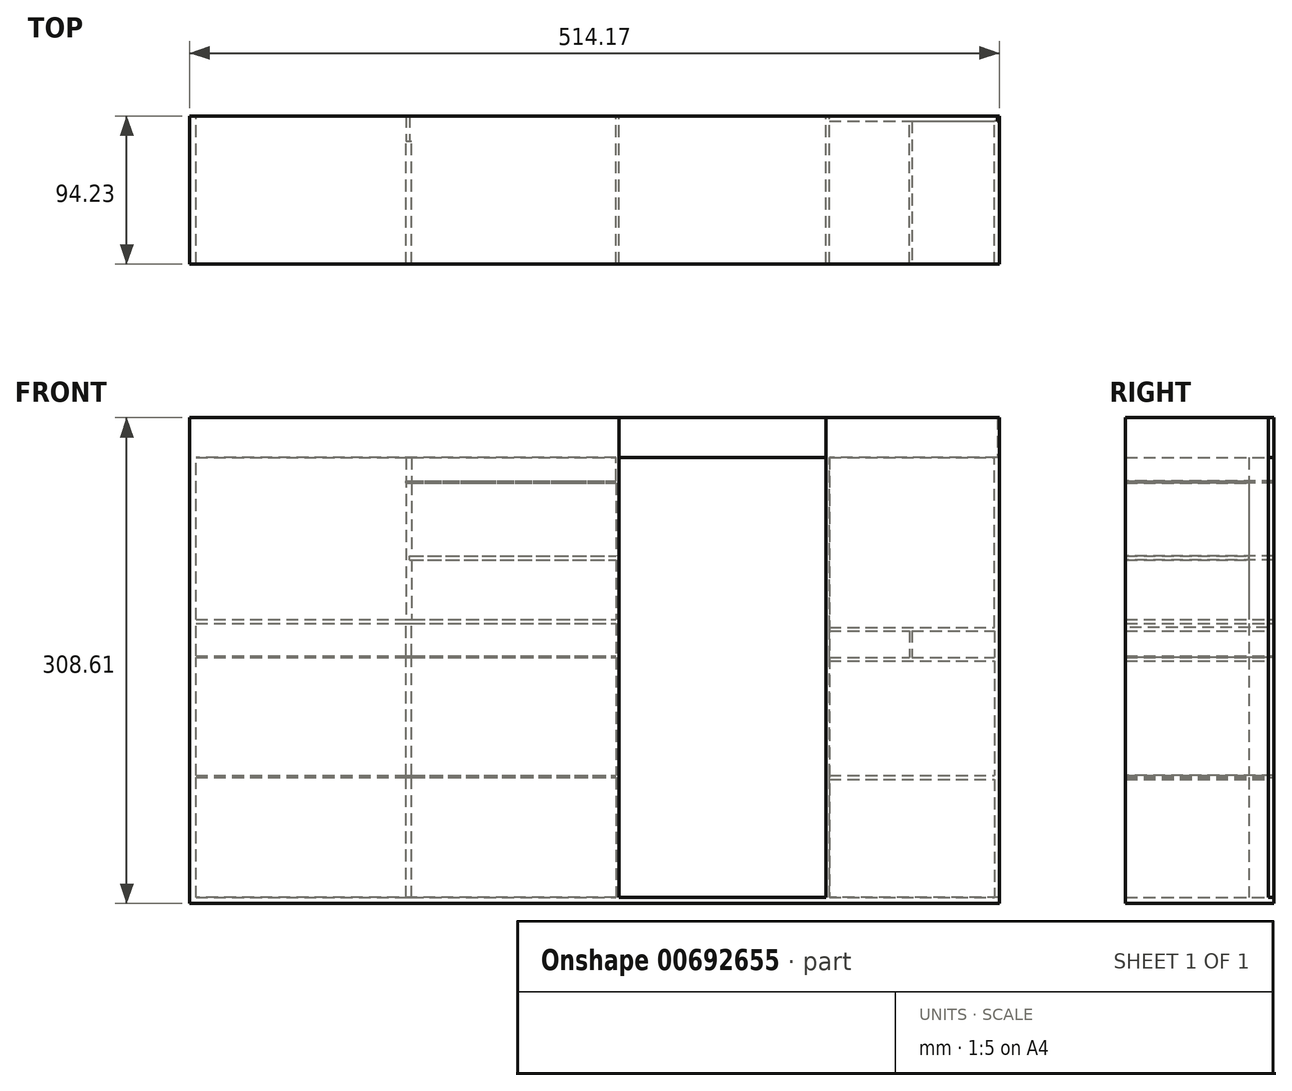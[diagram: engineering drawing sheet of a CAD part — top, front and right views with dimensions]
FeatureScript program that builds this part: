
annotation { "Feature Type Name" : "Feature", "Feature Type Description" : "" }
export const myFeature = defineFeature(function(context is Context, id is Id, definition is map)
    precondition{}
    {
        {
            var Q0;
            Q0=qCreatedBy(makeId("Top.planeOp"),FACE);
            var sketch = newSketch(context, id + "F0", { "sketchPlane" : qUnion([Q0])});
            skLineSegment(sketch, "E0.bottom", {"start": v(254.1, -132.08) * mm, "end": v(-260.07, -132.08) * mm});
            skLineSegment(sketch, "E0.top", {"start": v(254.1, -37.85) * mm, "end": v(-260.07, -37.85) * mm});
            skLineSegment(sketch, "E0.left", {"start": v(254.1, -132.08) * mm, "end": v(254.1, -37.85) * mm});
            skLineSegment(sketch, "E0.right", {"start": v(-260.07, -132.08) * mm, "end": v(-260.07, -37.85) * mm});
            skSolve(sketch);
        }
        {
            var Q0;
            Q0=makeQuery(id+"F0.imprint","IMPRINT",FACE,{"disambiguationData":[TD([[makeQuery(id+"F0.imprint","IMPRINT",EDGE,{"derivedFrom":sQuery(id+"F0.wireOp",EDGE,"E0.bottom")}),-1.0]])]});
            extrude(context, id + "F1", {"entities" : qUnion([Q0]), "depth" : 3.8 * mm, "offsetDistance" : 25.4 * mm});
        }
        {
            var Q0;
            Q0=makeQuery(id+"F1.opExtrude","CAP_FACE",FACE,{"disambiguationData":[OSD([sQuery(id+"F0.wireOp",EDGE,"E0.bottom"),sQuery(id+"F0.wireOp",EDGE,"E0.top"),sQuery(id+"F0.wireOp",EDGE,"E0.left"),sQuery(id+"F0.wireOp",EDGE,"E0.right")])],"isStart":false});
            var sketch = newSketch(context, id + "F2", { "sketchPlane" : qUnion([Q0])});
            skLineSegment(sketch, "E1.bottom", {"start": v(143.85, -132.08) * mm, "end": v(146.14, -132.08) * mm});
            skLineSegment(sketch, "E1.top", {"start": v(143.85, -37.85) * mm, "end": v(146.14, -37.85) * mm});
            skLineSegment(sketch, "E1.left", {"start": v(143.85, -132.08) * mm, "end": v(143.85, -37.85) * mm});
            skLineSegment(sketch, "E1.right", {"start": v(146.14, -132.08) * mm, "end": v(146.14, -37.85) * mm});
            skSolve(sketch);
        }
        {
            var Q0;
            Q0 = qSketchRegion(id + "F2", true);
            extrude(context, id + "F3", {"entities" : qUnion([Q0]), "operationType" : NewBodyOperationType.ADD, "depth" : 304.8 * mm, "offsetDistance" : 25.4 * mm});
        }
        {
            var Q0;
            {var subQ0=sQuery(id+"F0.wireOp",EDGE,"E0.left");var subQ1=sQuery(id+"F0.wireOp",EDGE,"E0.top");var subQ2=sQuery(id+"F0.wireOp",EDGE,"E0.bottom");Q0=makeQuery(id+"F3.boolean.opBoolean","SPLIT",FACE,{"disambiguationData":[TD([makeQuery(id+"F1.opExtrude","SWEPT_FACE",FACE,{"disambiguationData":[OSD([subQ0])]})])],"derivedFrom":makeQuery(id+"F1.opExtrude","CAP_FACE",FACE,{"disambiguationData":[OSD([subQ2,subQ1,subQ0,sQuery(id+"F0.wireOp",EDGE,"E0.right")])],"isStart":false})});}
            var sketch = newSketch(context, id + "F4", { "sketchPlane" : qUnion([Q0])});
            skLineSegment(sketch, "E2.bottom", {"start": v(254.1, -132.08) * mm, "end": v(250.9, -132.08) * mm});
            skLineSegment(sketch, "E2.top", {"start": v(254.1, -41.27) * mm, "end": v(250.9, -41.27) * mm});
            skLineSegment(sketch, "E2.left", {"start": v(254.1, -132.08) * mm, "end": v(254.1, -41.27) * mm});
            skLineSegment(sketch, "E2.right", {"start": v(250.9, -132.08) * mm, "end": v(250.9, -41.27) * mm});
            skSolve(sketch);
        }
        {
            var Q0;
            Q0 = qSketchRegion(id + "F4", true);
            extrude(context, id + "F5", {"entities" : qUnion([Q0]), "operationType" : NewBodyOperationType.ADD, "depth" : 304.8 * mm, "offsetDistance" : 25.4 * mm});
        }
        {
            var Q0;
            {var subQ0=sQuery(id+"F0.wireOp",EDGE,"E0.top");var subQ1=sQuery(id+"F0.wireOp",EDGE,"E0.right");var subQ2=sQuery(id+"F0.wireOp",EDGE,"E0.bottom");Q0=makeQuery(id+"F3.boolean.opBoolean","SPLIT",FACE,{"disambiguationData":[TD([makeQuery(id+"F1.opExtrude","SWEPT_FACE",FACE,{"disambiguationData":[OSD([subQ1])]})])],"derivedFrom":makeQuery(id+"F1.opExtrude","CAP_FACE",FACE,{"disambiguationData":[OSD([subQ2,subQ0,sQuery(id+"F0.wireOp",EDGE,"E0.left"),subQ1])],"isStart":false})});}
            var sketch = newSketch(context, id + "F6", { "sketchPlane" : qUnion([Q0])});
            skLineSegment(sketch, "E3.bottom", {"start": v(10.8, -132.08) * mm, "end": v(12.47, -132.08) * mm});
            skLineSegment(sketch, "E3.top", {"start": v(10.8, -37.85) * mm, "end": v(12.47, -37.85) * mm});
            skLineSegment(sketch, "E3.left", {"start": v(10.8, -132.08) * mm, "end": v(10.8, -37.85) * mm});
            skLineSegment(sketch, "E3.right", {"start": v(12.47, -132.08) * mm, "end": v(12.47, -37.85) * mm});
            skSolve(sketch);
        }
        {
            var Q0;
            Q0=makeQuery(id+"F6.imprint","IMPRINT",FACE,{"disambiguationData":[TD([[makeQuery(id+"F6.imprint","IMPRINT",EDGE,{"derivedFrom":sQuery(id+"F6.wireOp",EDGE,"E3.bottom")}),-1.0]])]});
            extrude(context, id + "F7", {"entities" : qUnion([Q0]), "operationType" : NewBodyOperationType.ADD, "depth" : 304.8 * mm, "offsetDistance" : 25.4 * mm});
        }
        {
            var Q0;
            {var subQ1=sQuery(id+"F0.wireOp",EDGE,"E0.top");var subQ3=sQuery(id+"F0.wireOp",EDGE,"E0.right");var subQ4=makeQuery(id+"F1.opExtrude","SWEPT_FACE",FACE,{"disambiguationData":[OSD([subQ3])]});var subQ5=sQuery(id+"F0.wireOp",EDGE,"E0.bottom");Q0=makeQuery(id+"F7.boolean.opBoolean","SPLIT",FACE,{"disambiguationData":[TD([subQ4])],"derivedFrom":makeQuery(id+"F3.boolean.opBoolean","SPLIT",FACE,{"disambiguationData":[TD([subQ4])],"derivedFrom":makeQuery(id+"F1.opExtrude","CAP_FACE",FACE,{"disambiguationData":[OSD([subQ5,subQ1,sQuery(id+"F0.wireOp",EDGE,"E0.left"),subQ3])],"isStart":false})})});}
            var sketch = newSketch(context, id + "F8", { "sketchPlane" : qUnion([Q0])});
            skLineSegment(sketch, "E4.bottom", {"start": v(-260.07, -132.08) * mm, "end": v(-256.21, -132.08) * mm});
            skLineSegment(sketch, "E4.top", {"start": v(-260.07, -37.85) * mm, "end": v(-256.21, -37.85) * mm});
            skLineSegment(sketch, "E4.left", {"start": v(-260.07, -132.08) * mm, "end": v(-260.07, -37.85) * mm});
            skLineSegment(sketch, "E4.right", {"start": v(-256.21, -132.08) * mm, "end": v(-256.21, -37.85) * mm});
            skSolve(sketch);
        }
        {
            var Q0;
            Q0 = qSketchRegion(id + "F8", true);
            extrude(context, id + "F9", {"entities" : qUnion([Q0]), "operationType" : NewBodyOperationType.ADD, "depth" : 304.8 * mm, "offsetDistance" : 25.4 * mm});
        }
        {
            var Q0;
            {var subQ1=sQuery(id+"F0.wireOp",EDGE,"E0.top");var subQ3=sQuery(id+"F0.wireOp",EDGE,"E0.right");var subQ4=makeQuery(id+"F1.opExtrude","SWEPT_FACE",FACE,{"disambiguationData":[OSD([subQ3])]});var subQ5=sQuery(id+"F0.wireOp",EDGE,"E0.bottom");Q0=makeQuery(id+"F7.boolean.opBoolean","SPLIT",FACE,{"disambiguationData":[TD([subQ4])],"derivedFrom":makeQuery(id+"F3.boolean.opBoolean","SPLIT",FACE,{"disambiguationData":[TD([subQ4])],"derivedFrom":makeQuery(id+"F1.opExtrude","CAP_FACE",FACE,{"disambiguationData":[OSD([subQ5,subQ1,sQuery(id+"F0.wireOp",EDGE,"E0.left"),subQ3])],"isStart":false})})});}
            var sketch = newSketch(context, id + "F10", { "sketchPlane" : qUnion([Q0])});
            skLineSegment(sketch, "E5.bottom", {"start": v(-122.7, -132.08) * mm, "end": v(-119.13, -132.08) * mm});
            skLineSegment(sketch, "E5.top", {"start": v(-122.7, -53.74) * mm, "end": v(-119.13, -53.74) * mm});
            skLineSegment(sketch, "E5.left", {"start": v(-122.7, -132.08) * mm, "end": v(-122.7, -53.74) * mm});
            skLineSegment(sketch, "E5.right", {"start": v(-119.13, -132.08) * mm, "end": v(-119.13, -53.74) * mm});
            skSolve(sketch);
        }
        {
            var Q0;
            Q0 = qSketchRegion(id + "F10", true);
            extrude(context, id + "F11", {"entities" : qUnion([Q0]), "operationType" : NewBodyOperationType.ADD, "depth" : 304.8 * mm, "offsetDistance" : 25.4 * mm});
        }
        {
            var Q0;
            Q0=makeQuery(id+"F11.boolean.opBoolean","MERGE",FACE,{"derivedFrom":[makeQuery(id+"F9.boolean.opBoolean","MERGE",FACE,{"derivedFrom":[makeQuery(id+"F7.boolean.opBoolean","MERGE",FACE,{"derivedFrom":[makeQuery(id+"F5.boolean.opBoolean","MERGE",FACE,{"derivedFrom":[makeQuery(id+"F3.boolean.opBoolean","MERGE",FACE,{"derivedFrom":[makeQuery(id+"F1.opExtrude","SWEPT_FACE",FACE,{"disambiguationData":[OSD([sQuery(id+"F0.wireOp",EDGE,"E0.bottom")])]}),makeQuery(id+"F3.opExtrude","SWEPT_FACE",FACE,{"disambiguationData":[OSD([sQuery(id+"F2.wireOp",EDGE,"E1.bottom")])]})]}),makeQuery(id+"F5.opExtrude","SWEPT_FACE",FACE,{"disambiguationData":[OSD([sQuery(id+"F4.wireOp",EDGE,"E2.bottom")])]})]}),makeQuery(id+"F7.opExtrude","SWEPT_FACE",FACE,{"disambiguationData":[OSD([sQuery(id+"F6.wireOp",EDGE,"E3.bottom")])]})]}),makeQuery(id+"F9.opExtrude","SWEPT_FACE",FACE,{"disambiguationData":[OSD([sQuery(id+"F8.wireOp",EDGE,"E4.bottom")])]})]}),makeQuery(id+"F11.opExtrude","SWEPT_FACE",FACE,{"disambiguationData":[OSD([sQuery(id+"F10.wireOp",EDGE,"E5.bottom")])]})]});
            var sketch = newSketch(context, id + "F12", { "sketchPlane" : qUnion([Q0])});
            skLineSegment(sketch, "E6.bottom", {"start": v(-260.07, 308.6) * mm, "end": v(12.47, 308.6) * mm});
            skLineSegment(sketch, "E6.top", {"start": v(-260.07, 0) * mm, "end": v(12.47, 0) * mm});
            skLineSegment(sketch, "E6.left", {"start": v(-260.07, 308.6) * mm, "end": v(-260.07, 0) * mm});
            skLineSegment(sketch, "E6.right", {"start": v(12.47, 308.6) * mm, "end": v(12.47, 0) * mm});
            skSolve(sketch);
        }
        {
            var Q0;
            Q0 = qSketchRegion(id + "F12", true);
            extrude(context, id + "F13", {"entities" : qUnion([Q0]), "operationType" : NewBodyOperationType.ADD, "oppositeDirection" : true, "depth" : 0.25 * mm, "offsetDistance" : 25.4 * mm});
        }
        {
            var Q0;
            Q0=makeQuery(id+"F13.boolean.opBoolean","MERGE",FACE,{"derivedFrom":[makeQuery(id+"F11.boolean.opBoolean","MERGE",FACE,{"derivedFrom":[makeQuery(id+"F9.boolean.opBoolean","MERGE",FACE,{"derivedFrom":[makeQuery(id+"F7.boolean.opBoolean","MERGE",FACE,{"derivedFrom":[makeQuery(id+"F5.boolean.opBoolean","MERGE",FACE,{"derivedFrom":[makeQuery(id+"F3.boolean.opBoolean","MERGE",FACE,{"derivedFrom":[makeQuery(id+"F1.opExtrude","SWEPT_FACE",FACE,{"disambiguationData":[OSD([sQuery(id+"F0.wireOp",EDGE,"E0.bottom")])]}),makeQuery(id+"F3.opExtrude","SWEPT_FACE",FACE,{"disambiguationData":[OSD([sQuery(id+"F2.wireOp",EDGE,"E1.bottom")])]})]}),makeQuery(id+"F5.opExtrude","SWEPT_FACE",FACE,{"disambiguationData":[OSD([sQuery(id+"F4.wireOp",EDGE,"E2.bottom")])]})]}),makeQuery(id+"F7.opExtrude","SWEPT_FACE",FACE,{"disambiguationData":[OSD([sQuery(id+"F6.wireOp",EDGE,"E3.bottom")])]})]}),makeQuery(id+"F9.opExtrude","SWEPT_FACE",FACE,{"disambiguationData":[OSD([sQuery(id+"F8.wireOp",EDGE,"E4.bottom")])]})]}),makeQuery(id+"F11.opExtrude","SWEPT_FACE",FACE,{"disambiguationData":[OSD([sQuery(id+"F10.wireOp",EDGE,"E5.bottom")])]})]}),makeQuery(id+"F13.opExtrude","CAP_FACE",FACE,{"disambiguationData":[OSD([sQuery(id+"F12.wireOp",EDGE,"E6.bottom"),sQuery(id+"F12.wireOp",EDGE,"E6.top"),sQuery(id+"F12.wireOp",EDGE,"E6.left"),sQuery(id+"F12.wireOp",EDGE,"E6.right")])],"isStart":true})]});
            var sketch = newSketch(context, id + "F14", { "sketchPlane" : qUnion([Q0])});
            skLineSegment(sketch, "E7.bottom", {"start": v(143.85, 308.6) * mm, "end": v(254.1, 308.6) * mm});
            skLineSegment(sketch, "E7.top", {"start": v(143.85, 0) * mm, "end": v(254.1, 0) * mm});
            skLineSegment(sketch, "E7.left", {"start": v(143.85, 308.6) * mm, "end": v(143.85, 0) * mm});
            skLineSegment(sketch, "E7.right", {"start": v(254.1, 308.6) * mm, "end": v(254.1, 0) * mm});
            skSolve(sketch);
        }
        {
            var Q0;
            Q0 = qSketchRegion(id + "F14", true);
            extrude(context, id + "F15", {"entities" : qUnion([Q0]), "operationType" : NewBodyOperationType.ADD, "oppositeDirection" : true, "depth" : 0.25 * mm, "offsetDistance" : 25.4 * mm});
        }
        {
            var Q0;
            Q0=makeQuery(id+"F5.opExtrude","SWEPT_FACE",FACE,{"disambiguationData":[OSD([sQuery(id+"F4.wireOp",EDGE,"E2.right")])]});
            var sketch = newSketch(context, id + "F16", { "sketchPlane" : qUnion([Q0])});
            skLineSegment(sketch, "E8.bottom", {"start": v(41.27, 156.21) * mm, "end": v(131.83, 156.21) * mm});
            skLineSegment(sketch, "E8.top", {"start": v(41.27, 154.06) * mm, "end": v(131.83, 154.06) * mm});
            skLineSegment(sketch, "E8.left", {"start": v(41.27, 156.21) * mm, "end": v(41.27, 154.06) * mm});
            skLineSegment(sketch, "E8.right", {"start": v(131.83, 156.21) * mm, "end": v(131.83, 154.06) * mm});
            skSolve(sketch);
        }
        {
            var Q0;
            Q0 = qSketchRegion(id + "F16", true);
            extrude(context, id + "F17", {"entities" : qUnion([Q0]), "operationType" : NewBodyOperationType.ADD, "depth" : 105.4 * mm, "offsetDistance" : 25.4 * mm});
        }
        {
            var Q0;
            Q0=makeQuery(id+"F17.boolean.opBoolean","SPLIT",FACE,{"disambiguationData":[TD([makeQuery(id+"F17.opExtrude","SWEPT_FACE",FACE,{"disambiguationData":[OSD([sQuery(id+"F16.wireOp",EDGE,"E8.top")])]})])],"derivedFrom":makeQuery(id+"F5.opExtrude","SWEPT_FACE",FACE,{"disambiguationData":[OSD([sQuery(id+"F4.wireOp",EDGE,"E2.right")])]})});
            var sketch = newSketch(context, id + "F18", { "sketchPlane" : qUnion([Q0])});
            skLineSegment(sketch, "E9.bottom", {"start": v(41.27, 78.93) * mm, "end": v(131.83, 78.93) * mm});
            skLineSegment(sketch, "E9.top", {"start": v(41.27, 81.34) * mm, "end": v(131.83, 81.34) * mm});
            skLineSegment(sketch, "E9.left", {"start": v(41.27, 78.93) * mm, "end": v(41.27, 81.34) * mm});
            skLineSegment(sketch, "E9.right", {"start": v(131.83, 78.93) * mm, "end": v(131.83, 81.34) * mm});
            skSolve(sketch);
        }
        {
            var Q0;
            Q0 = qSketchRegion(id + "F18", true);
            extrude(context, id + "F19", {"entities" : qUnion([Q0]), "operationType" : NewBodyOperationType.ADD, "depth" : 106.93 * mm, "offsetDistance" : 25.4 * mm});
        }
        {
            var Q0;
            {var subQ0=sQuery(id+"F14.wireOp",EDGE,"E7.bottom");var subQ2=sQuery(id+"F4.wireOp",EDGE,"E2.right");Q0=makeQuery(id+"F17.boolean.opBoolean","SPLIT",FACE,{"disambiguationData":[TD([makeQuery(id+"F15.opExtrude","SWEPT_FACE",FACE,{"disambiguationData":[OSD([subQ0])]})])],"derivedFrom":makeQuery(id+"F5.opExtrude","SWEPT_FACE",FACE,{"disambiguationData":[OSD([subQ2])]})});}
            var sketch = newSketch(context, id + "F20", { "sketchPlane" : qUnion([Q0])});
            skLineSegment(sketch, "E10.bottom", {"start": v(41.27, 173.32) * mm, "end": v(131.83, 173.32) * mm});
            skLineSegment(sketch, "E10.top", {"start": v(41.27, 175.5) * mm, "end": v(131.83, 175.5) * mm});
            skLineSegment(sketch, "E10.left", {"start": v(41.27, 173.32) * mm, "end": v(41.27, 175.5) * mm});
            skLineSegment(sketch, "E10.right", {"start": v(131.83, 173.32) * mm, "end": v(131.83, 175.5) * mm});
            skSolve(sketch);
        }
        {
            var Q0;
            Q0 = qSketchRegion(id + "F20", true);
            extrude(context, id + "F21", {"entities" : qUnion([Q0]), "operationType" : NewBodyOperationType.ADD, "depth" : 106.93 * mm, "offsetDistance" : 25.4 * mm});
        }
        {
            var Q0;
            Q0=makeQuery(id+"F17.opExtrude","SWEPT_FACE",FACE,{"disambiguationData":[OSD([sQuery(id+"F16.wireOp",EDGE,"E8.bottom")])]});
            var sketch = newSketch(context, id + "F22", { "sketchPlane" : qUnion([Q0])});
            skLineSegment(sketch, "E11.bottom", {"start": v(198.51, -131.83) * mm, "end": v(197.02, -131.83) * mm});
            skLineSegment(sketch, "E11.top", {"start": v(198.51, -41.27) * mm, "end": v(197.02, -41.27) * mm});
            skLineSegment(sketch, "E11.left", {"start": v(198.51, -131.83) * mm, "end": v(198.51, -41.27) * mm});
            skLineSegment(sketch, "E11.right", {"start": v(197.02, -131.83) * mm, "end": v(197.02, -41.27) * mm});
            skSolve(sketch);
        }
        {
            var Q0;
            Q0 = qSketchRegion(id + "F22", true);
            extrude(context, id + "F23", {"entities" : qUnion([Q0]), "operationType" : NewBodyOperationType.ADD, "depth" : 18.54 * mm, "offsetDistance" : 25.4 * mm});
        }
        {
            var Q0;
            {var subQ0=sQuery(id+"F14.wireOp",EDGE,"E7.bottom");var subQ1=makeQuery(id+"F15.opExtrude","SWEPT_FACE",FACE,{"disambiguationData":[OSD([subQ0])]});var subQ4=sQuery(id+"F4.wireOp",EDGE,"E2.right");Q0=makeQuery(id+"F21.boolean.opBoolean","SPLIT",FACE,{"disambiguationData":[TD([subQ1])],"derivedFrom":makeQuery(id+"F17.boolean.opBoolean","SPLIT",FACE,{"disambiguationData":[TD([subQ1])],"derivedFrom":makeQuery(id+"F5.opExtrude","SWEPT_FACE",FACE,{"disambiguationData":[OSD([subQ4])]})})});}
            var sketch = newSketch(context, id + "F24", { "sketchPlane" : qUnion([Q0])});
            skCircle(sketch, "E12", {"center": v(86.55, 288.23) * mm, "radius": 2.79 * mm});
            skPoint(sketch, "E12.centerSnap0", {"position": v(86.55, 308.6) * mm});
            skSolve(sketch);
        }
        {
            var Q0;
            Q0 = qSketchRegion(id + "F24", true);
            extrude(context, id + "F25", {"entities" : qUnion([Q0]), "operationType" : NewBodyOperationType.ADD, "depth" : 106.68 * mm, "offsetDistance" : 25.4 * mm});
        }
        {
            var Q0;
            Q0=makeQuery(id+"F7.opExtrude","SWEPT_FACE",FACE,{"disambiguationData":[OSD([sQuery(id+"F6.wireOp",EDGE,"E3.left")])]});
            var sketch = newSketch(context, id + "F26", { "sketchPlane" : qUnion([Q0])});
            skLineSegment(sketch, "E13.bottom", {"start": v(37.85, 156.21) * mm, "end": v(131.83, 156.21) * mm});
            skLineSegment(sketch, "E13.top", {"start": v(37.85, 157.38) * mm, "end": v(131.83, 157.38) * mm});
            skLineSegment(sketch, "E13.left", {"start": v(37.85, 156.21) * mm, "end": v(37.85, 157.38) * mm});
            skLineSegment(sketch, "E13.right", {"start": v(131.83, 156.21) * mm, "end": v(131.83, 157.38) * mm});
            skSolve(sketch);
        }
        {
            var Q0;
            Q0 = qSketchRegion(id + "F26", true);
            extrude(context, id + "F27", {"entities" : qUnion([Q0]), "operationType" : NewBodyOperationType.ADD, "depth" : 268.22 * mm, "offsetDistance" : 25.4 * mm});
        }
        {
            var Q0;
            {var subQ0=sQuery(id+"F12.wireOp",EDGE,"E6.bottom");var subQ2=sQuery(id+"F6.wireOp",EDGE,"E3.left");Q0=makeQuery(id+"F27.boolean.opBoolean","SPLIT",FACE,{"disambiguationData":[TD([makeQuery(id+"F13.opExtrude","SWEPT_FACE",FACE,{"disambiguationData":[OSD([subQ0])]})])],"derivedFrom":makeQuery(id+"F7.opExtrude","SWEPT_FACE",FACE,{"disambiguationData":[OSD([subQ2])]})});}
            var sketch = newSketch(context, id + "F28", { "sketchPlane" : qUnion([Q0])});
            skLineSegment(sketch, "E14.bottom", {"start": v(37.85, 180.36) * mm, "end": v(131.83, 180.36) * mm});
            skLineSegment(sketch, "E14.top", {"start": v(37.85, 177.81) * mm, "end": v(131.83, 177.81) * mm});
            skLineSegment(sketch, "E14.left", {"start": v(37.85, 180.36) * mm, "end": v(37.85, 177.81) * mm});
            skLineSegment(sketch, "E14.right", {"start": v(131.83, 180.36) * mm, "end": v(131.83, 177.81) * mm});
            skSolve(sketch);
        }
        {
            var Q0;
            Q0 = qSketchRegion(id + "F28", true);
            extrude(context, id + "F29", {"entities" : qUnion([Q0]), "operationType" : NewBodyOperationType.ADD, "depth" : 270.26 * mm, "offsetDistance" : 25.4 * mm});
        }
        {
            var Q0;
            Q0=makeQuery(id+"F27.boolean.opBoolean","SPLIT",FACE,{"disambiguationData":[TD([makeQuery(id+"F27.opExtrude","SWEPT_FACE",FACE,{"disambiguationData":[OSD([sQuery(id+"F26.wireOp",EDGE,"E13.bottom")])]})])],"derivedFrom":makeQuery(id+"F7.opExtrude","SWEPT_FACE",FACE,{"disambiguationData":[OSD([sQuery(id+"F6.wireOp",EDGE,"E3.left")])]})});
            var sketch = newSketch(context, id + "F30", { "sketchPlane" : qUnion([Q0])});
            skLineSegment(sketch, "E15.bottom", {"start": v(37.85, 80.01) * mm, "end": v(131.83, 80.01) * mm});
            skLineSegment(sketch, "E15.top", {"start": v(37.85, 81.29) * mm, "end": v(131.83, 81.29) * mm});
            skLineSegment(sketch, "E15.left", {"start": v(37.85, 80.01) * mm, "end": v(37.85, 81.29) * mm});
            skLineSegment(sketch, "E15.right", {"start": v(131.83, 80.01) * mm, "end": v(131.83, 81.29) * mm});
            skSolve(sketch);
        }
        {
            var Q0;
            Q0 = qSketchRegion(id + "F30", true);
            extrude(context, id + "F31", {"entities" : qUnion([Q0]), "operationType" : NewBodyOperationType.ADD, "depth" : 269.24 * mm, "offsetDistance" : 25.4 * mm});
        }
        {
            var Q0;
            {var subQ2=sQuery(id+"F12.wireOp",EDGE,"E6.bottom");var subQ7=makeQuery(id+"F13.opExtrude","SWEPT_FACE",FACE,{"disambiguationData":[OSD([subQ2])]});var subQ9=sQuery(id+"F6.wireOp",EDGE,"E3.left");Q0=makeQuery(id+"F29.boolean.opBoolean","SPLIT",FACE,{"disambiguationData":[TD([subQ7])],"derivedFrom":makeQuery(id+"F27.boolean.opBoolean","SPLIT",FACE,{"disambiguationData":[TD([subQ7])],"derivedFrom":makeQuery(id+"F7.opExtrude","SWEPT_FACE",FACE,{"disambiguationData":[OSD([subQ9])]})})});}
            var sketch = newSketch(context, id + "F32", { "sketchPlane" : qUnion([Q0])});
            skLineSegment(sketch, "E16.bottom", {"start": v(37.85, 268.45) * mm, "end": v(131.83, 268.45) * mm});
            skLineSegment(sketch, "E16.top", {"start": v(37.85, 267.11) * mm, "end": v(131.83, 267.11) * mm});
            skLineSegment(sketch, "E16.left", {"start": v(37.85, 268.45) * mm, "end": v(37.85, 267.11) * mm});
            skLineSegment(sketch, "E16.right", {"start": v(131.83, 268.45) * mm, "end": v(131.83, 267.11) * mm});
            skSolve(sketch);
        }
        {
            var Q0;
            Q0 = qSketchRegion(id + "F32", true);
            extrude(context, id + "F33", {"entities" : qUnion([Q0]), "operationType" : NewBodyOperationType.ADD, "depth" : 133.35 * mm, "offsetDistance" : 25.4 * mm});
        }
        {
            var Q0;
            {var subQ0=makeQuery(id+"F29.opExtrude","SWEPT_FACE",FACE,{"disambiguationData":[OSD([sQuery(id+"F28.wireOp",EDGE,"E14.bottom")])]});var subQ3=sQuery(id+"F12.wireOp",EDGE,"E6.bottom");var subQ12=makeQuery(id+"F13.opExtrude","SWEPT_FACE",FACE,{"disambiguationData":[OSD([subQ3])]});var subQ14=sQuery(id+"F6.wireOp",EDGE,"E3.left");Q0=makeQuery(id+"F33.boolean.opBoolean","SPLIT",FACE,{"disambiguationData":[TD([subQ0])],"derivedFrom":makeQuery(id+"F29.boolean.opBoolean","SPLIT",FACE,{"disambiguationData":[TD([subQ12])],"derivedFrom":makeQuery(id+"F27.boolean.opBoolean","SPLIT",FACE,{"disambiguationData":[TD([subQ12])],"derivedFrom":makeQuery(id+"F7.opExtrude","SWEPT_FACE",FACE,{"disambiguationData":[OSD([subQ14])]})})})});}
            var sketch = newSketch(context, id + "F34", { "sketchPlane" : qUnion([Q0])});
            skLineSegment(sketch, "E17.bottom", {"start": v(37.85, 218.4) * mm, "end": v(131.83, 218.4) * mm});
            skLineSegment(sketch, "E17.top", {"start": v(37.85, 220.84) * mm, "end": v(131.83, 220.84) * mm});
            skLineSegment(sketch, "E17.left", {"start": v(37.85, 218.4) * mm, "end": v(37.85, 220.84) * mm});
            skLineSegment(sketch, "E17.right", {"start": v(131.83, 218.4) * mm, "end": v(131.83, 220.84) * mm});
            skSolve(sketch);
        }
        {
            var Q0;
            Q0 = qSketchRegion(id + "F34", true);
            extrude(context, id + "F35", {"entities" : qUnion([Q0]), "operationType" : NewBodyOperationType.ADD, "depth" : 131.32 * mm, "offsetDistance" : 25.4 * mm});
        }
        {
            var Q0;
            {var subQ0=sQuery(id+"F10.wireOp",EDGE,"E5.left");var subQ6=sQuery(id+"F12.wireOp",EDGE,"E6.bottom");var subQ7=makeQuery(id+"F13.opExtrude","SWEPT_FACE",FACE,{"disambiguationData":[OSD([subQ6])]});Q0=makeQuery(id+"F29.boolean.opBoolean","SPLIT",FACE,{"disambiguationData":[TD([subQ7])],"derivedFrom":makeQuery(id+"F27.boolean.opBoolean","SPLIT",FACE,{"disambiguationData":[TD([subQ7])],"derivedFrom":makeQuery(id+"F11.opExtrude","SWEPT_FACE",FACE,{"disambiguationData":[OSD([subQ0])]})})});}
            var sketch = newSketch(context, id + "F36", { "sketchPlane" : qUnion([Q0])});
            skCircle(sketch, "E18", {"center": v(94.45, 294.7) * mm, "radius": 1.65 * mm});
            skSolve(sketch);
        }
        {
            var Q0;
            Q0 = qSketchRegion(id + "F36", true);
            extrude(context, id + "F37", {"entities" : qUnion([Q0]), "operationType" : NewBodyOperationType.ADD, "depth" : 136.9 * mm, "offsetDistance" : 25.4 * mm});
        }
        {
            var Q0;
            Q0=makeQuery(id+"F13.boolean.opBoolean","MERGE",FACE,{"derivedFrom":[makeQuery(id+"F7.opExtrude","CAP_FACE",FACE,{"disambiguationData":[OSD([sQuery(id+"F6.wireOp",EDGE,"E3.bottom"),sQuery(id+"F6.wireOp",EDGE,"E3.top"),sQuery(id+"F6.wireOp",EDGE,"E3.left"),sQuery(id+"F6.wireOp",EDGE,"E3.right")])],"isStart":false}),makeQuery(id+"F9.opExtrude","CAP_FACE",FACE,{"disambiguationData":[OSD([sQuery(id+"F8.wireOp",EDGE,"E4.bottom"),sQuery(id+"F8.wireOp",EDGE,"E4.top"),sQuery(id+"F8.wireOp",EDGE,"E4.left"),sQuery(id+"F8.wireOp",EDGE,"E4.right")])],"isStart":false}),makeQuery(id+"F11.opExtrude","CAP_FACE",FACE,{"disambiguationData":[OSD([sQuery(id+"F10.wireOp",EDGE,"E5.bottom"),sQuery(id+"F10.wireOp",EDGE,"E5.top"),sQuery(id+"F10.wireOp",EDGE,"E5.left"),sQuery(id+"F10.wireOp",EDGE,"E5.right")])],"isStart":false}),makeQuery(id+"F13.opExtrude","SWEPT_FACE",FACE,{"disambiguationData":[OSD([sQuery(id+"F12.wireOp",EDGE,"E6.bottom")])]})]});
            var sketch = newSketch(context, id + "F38", { "sketchPlane" : qUnion([Q0])});
            skLineSegment(sketch, "E19.bottom", {"start": v(-260.07, -37.85) * mm, "end": v(252.9, -37.85) * mm});
            skLineSegment(sketch, "E19.top", {"start": v(-260.07, -131.83) * mm, "end": v(252.9, -131.83) * mm});
            skLineSegment(sketch, "E19.left", {"start": v(-260.07, -37.85) * mm, "end": v(-260.07, -131.83) * mm});
            skLineSegment(sketch, "E19.right", {"start": v(252.9, -37.85) * mm, "end": v(252.9, -131.83) * mm});
            skSolve(sketch);
        }
        {
            var Q0;
            Q0 = qSketchRegion(id + "F38", true);
            extrude(context, id + "F39", {"entities" : qUnion([Q0]), "operationType" : NewBodyOperationType.ADD, "oppositeDirection" : true, "depth" : 25.4 * mm, "offsetDistance" : 25.4 * mm});
        }
    });
